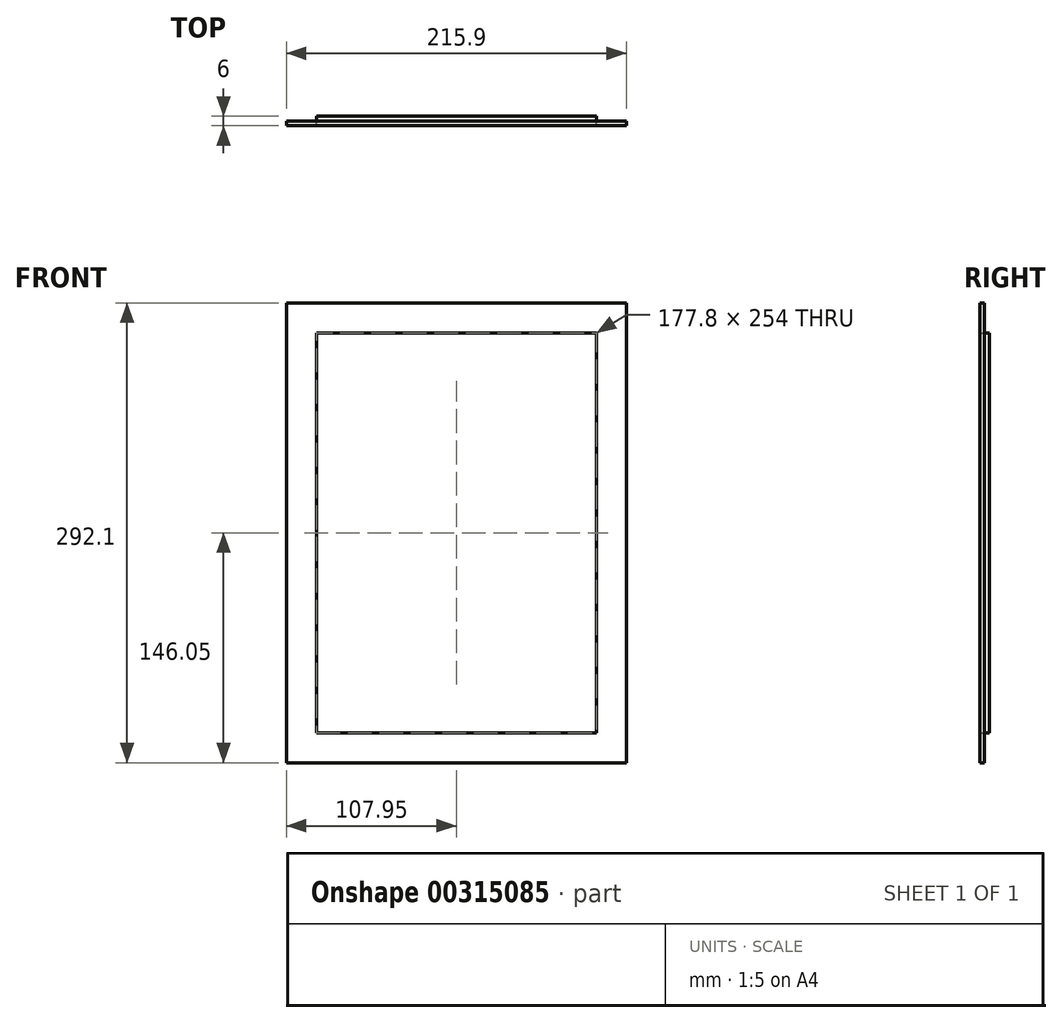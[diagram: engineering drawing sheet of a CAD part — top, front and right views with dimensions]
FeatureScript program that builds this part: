
annotation { "Feature Type Name" : "Feature", "Feature Type Description" : "" }
export const myFeature = defineFeature(function(context is Context, id is Id, definition is map)
    precondition{}
    {
        {
            var Q0;
            Q0=qCreatedBy(makeId("Front.planeOp"),FACE);
            var sketch = newSketch(context, id + "F0", { "sketchPlane" : qUnion([Q0])});
            skLineSegment(sketch, "E0.bottom", {"start": v(-110.99, 139.42) * mm, "end": v(66.81, 139.42) * mm});
            skLineSegment(sketch, "E0.top", {"start": v(-110.99, -114.58) * mm, "end": v(66.81, -114.58) * mm});
            skLineSegment(sketch, "E0.left", {"start": v(-110.99, 139.42) * mm, "end": v(-110.99, -114.58) * mm});
            skLineSegment(sketch, "E0.right", {"start": v(66.81, 139.42) * mm, "end": v(66.81, -114.58) * mm});
            skSolve(sketch);
        }
        {
            var Q0;
            Q0 = qSketchRegion(id + "F0", true);
            extrude(context, id + "F1", {"entities" : qUnion([Q0]), "depth" : 3 * mm});
        }
        {
            var Q0;
            Q0=makeQuery(id+"F1.opExtrude","CAP_FACE",FACE,{"disambiguationData":[OSD([sQuery(id+"F0.wireOp",EDGE,"E0.bottom"),sQuery(id+"F0.wireOp",EDGE,"E0.top"),sQuery(id+"F0.wireOp",EDGE,"E0.left"),sQuery(id+"F0.wireOp",EDGE,"E0.right")])],"isStart":false});
            var sketch = newSketch(context, id + "F2", { "sketchPlane" : qUnion([Q0])});
            skLineSegment(sketch, "E1.bottom", {"start": v(-130.04, 158.47) * mm, "end": v(85.86, 158.47) * mm});
            skLineSegment(sketch, "E1.top", {"start": v(-130.04, -133.63) * mm, "end": v(85.86, -133.63) * mm});
            skLineSegment(sketch, "E1.left", {"start": v(-130.04, 158.47) * mm, "end": v(-130.04, -133.63) * mm});
            skLineSegment(sketch, "E1.right", {"start": v(85.86, 158.47) * mm, "end": v(85.86, -133.63) * mm});
            skLineSegment(sketch, "E2.0.0", {"start": v(-110.99, 139.42) * mm, "end": v(-110.99, -114.58) * mm});
            skLineSegment(sketch, "E2.0.1", {"start": v(-110.99, -114.58) * mm, "end": v(66.81, -114.58) * mm});
            skLineSegment(sketch, "E2.0.2", {"start": v(66.81, -114.58) * mm, "end": v(66.81, 139.42) * mm});
            skLineSegment(sketch, "E2.0.3", {"start": v(66.81, 139.42) * mm, "end": v(-110.99, 139.42) * mm});
            skSolve(sketch);
        }
        {
            var Q0;
            Q0 = qSketchRegion(id + "F2", true);
            extrude(context, id + "F3", {"entities" : qUnion([Q0]), "depth" : 3 * mm});
        }
    });
